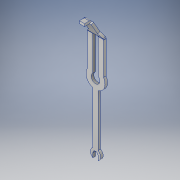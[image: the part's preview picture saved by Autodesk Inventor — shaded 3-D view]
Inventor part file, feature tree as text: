
AUTODESK INVENTOR PART (.ipt)
format: ipt  version: 2018 (Build 220112000, 112)  size: 180,224 bytes
history: native  units: in
note: dims shown in document units (in); Inventor stores cm internally (conversion verified against a paired STEP export)
features: sketch x3, other x2, extrude x1, plane x1
ambient origin geometry x8: Origin, YZ Plane, XZ Plane, XY Plane, X Axis, Y Axis, Z Axis, Center Point
bodies: Solid1 (feature_tree)
feature tree (7):
  extrude  "Extrusion1"  Depth=0.159in
  other  "Bend Part1"
  plane  "Work Plane1"
  other  "Bend Part2"
  sketch  "Sketch1"  dims[d0=0.08in d1=0.159in]
  sketch  "Sketch2"  dims[d3=0.8in]
  sketch  "Sketch3"  dims[d5=0.08in d6=0.135in d8=0.25in d9=0.5in d10=0.085in d11=0.14in d12=0.2in d13=0.08in d14=0.08in d15=0.04in d16=0.0in d17=0.05in d18=30.0deg d19=0.0in d20=0.0in d21=60.0deg]
